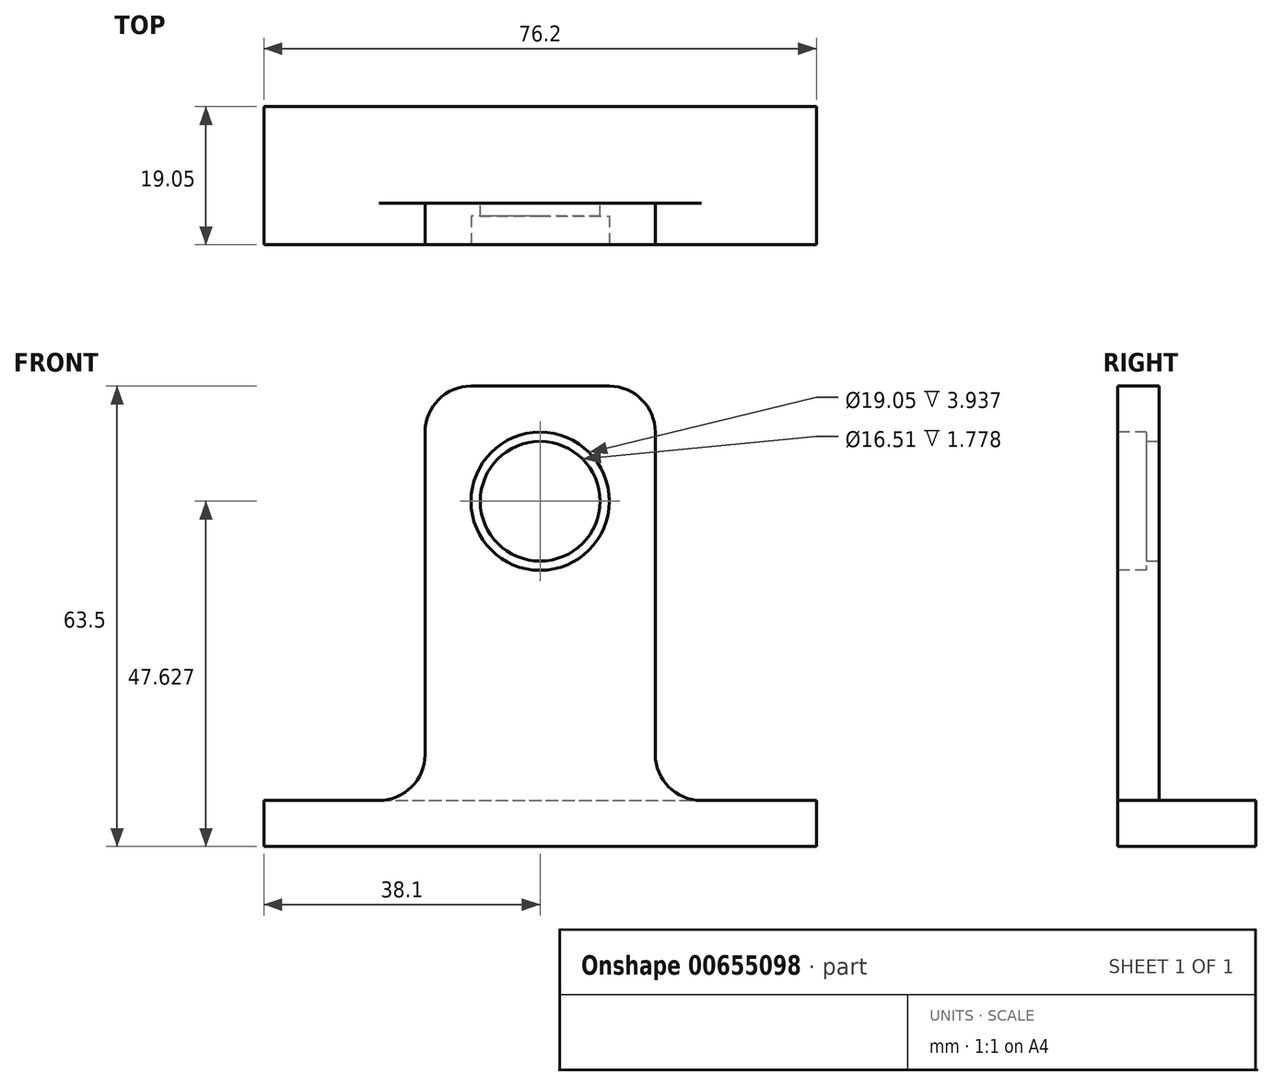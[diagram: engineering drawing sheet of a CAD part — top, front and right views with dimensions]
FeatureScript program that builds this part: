
annotation { "Feature Type Name" : "Feature", "Feature Type Description" : "" }
export const myFeature = defineFeature(function(context is Context, id is Id, definition is map)
    precondition{}
    {
        {
            var Q0;
            Q0=qCreatedBy(makeId("Front.planeOp"),FACE);
            var sketch = newSketch(context, id + "F0", { "sketchPlane" : qUnion([Q0])});
            skLineSegment(sketch, "E0.bottom", {"start": v(-38.1, -49.67) * mm, "end": v(38.1, -49.67) * mm});
            skLineSegment(sketch, "E0.top", {"start": v(22.23, -43.32) * mm, "end": v(38.1, -43.32) * mm});
            skLineSegment(sketch, "E0.left", {"start": v(-38.1, -49.67) * mm, "end": v(-38.1, -43.32) * mm});
            skLineSegment(sketch, "E0.right", {"start": v(38.1, -49.67) * mm, "end": v(38.1, -43.32) * mm});
            skLineSegment(sketch, "E1.top", {"start": v(-9.53, 13.83) * mm, "end": v(9.52, 13.83) * mm});
            skLineSegment(sketch, "E1.left", {"start": v(-15.87, -36.97) * mm, "end": v(-15.88, 7.48) * mm});
            skLineSegment(sketch, "E1.right", {"start": v(15.88, -36.97) * mm, "end": v(15.88, 7.48) * mm});
            skPoint(sketch, "E2.visualSharp", {"position": v(-15.88, 13.83) * mm});
            skArc(sketch, "E2.filletArc", {"start": v(-9.53, 13.83) * mm, "mid": v(-14.02, 11.97) * mm, "end": v(-15.88, 7.48) * mm});
            skPoint(sketch, "E3.visualSharp", {"position": v(15.88, 13.83) * mm});
            skArc(sketch, "E3.filletArc", {"start": v(15.88, 7.48) * mm, "mid": v(14.02, 11.97) * mm, "end": v(9.52, 13.83) * mm});
            skArc(sketch, "E4.filletArc", {"start": v(15.88, -36.97) * mm, "mid": v(17.73, -41.46) * mm, "end": v(22.23, -43.32) * mm});
            skLineSegment(sketch, "E5", {"start": v(-38.1, -43.32) * mm, "end": v(-22.22, -43.32) * mm});
            skPoint(sketch, "E6.visualSharp", {"position": v(-15.87, -43.32) * mm});
            skArc(sketch, "E6.filletArc", {"start": v(-22.22, -43.32) * mm, "mid": v(-17.73, -41.46) * mm, "end": v(-15.87, -36.97) * mm});
            skSolve(sketch);
        }
        {
            var Q0;
            Q0 = qSketchRegion(id + "F0", true);
            extrude(context, id + "F1", {"entities" : qUnion([Q0]), "depth" : 19.05 * mm, "offsetDistance" : 25.4 * mm});
        }
        {
            var Q0;
            Q0=qCreatedBy(makeId("Right.planeOp"),FACE);
            var sketch = newSketch(context, id + "F2", { "sketchPlane" : qUnion([Q0])});
            skLineSegment(sketch, "E7.bottom", {"start": v(-13.33, -43.32) * mm, "end": v(12.83, -43.32) * mm});
            skLineSegment(sketch, "E7.top", {"start": v(-13.34, 13.83) * mm, "end": v(12.83, 13.83) * mm});
            skLineSegment(sketch, "E7.left", {"start": v(-13.33, -43.32) * mm, "end": v(-13.34, 13.83) * mm});
            skLineSegment(sketch, "E7.right", {"start": v(12.83, -43.32) * mm, "end": v(12.83, 13.83) * mm});
            skSolve(sketch);
        }
        {
            var Q0;
            Q0 = qSketchRegion(id + "F2", true);
            extrude(context, id + "F3", {"entities" : qUnion([Q0]), "operationType" : NewBodyOperationType.REMOVE, "endBound" : BoundingType.THROUGH_ALL, "oppositeDirection" : true, "depth" : 25.4 * mm, "offsetDistance" : 25.4 * mm, "hasSecondDirection" : true, "secondDirectionBound" : SecondDirectionBoundingType.THROUGH_ALL, "secondDirectionOppositeDirection" : false, "secondDirectionDepth" : 25.4 * mm});
        }
        {
            var Q0;
            Q0=makeQuery(id+"F1.opExtrude","CAP_FACE",FACE,{"disambiguationData":[OSD([sQuery(id+"F0.wireOp",EDGE,"E0.bottom"),sQuery(id+"F0.wireOp",EDGE,"E0.top"),sQuery(id+"F0.wireOp",EDGE,"E0.left"),sQuery(id+"F0.wireOp",EDGE,"E0.right"),sQuery(id+"F0.wireOp",EDGE,"E1.top"),sQuery(id+"F0.wireOp",EDGE,"E1.left"),sQuery(id+"F0.wireOp",EDGE,"E1.right"),sQuery(id+"F0.wireOp",EDGE,"E2.filletArc"),sQuery(id+"F0.wireOp",EDGE,"E3.filletArc"),sQuery(id+"F0.wireOp",EDGE,"E4.filletArc"),sQuery(id+"F0.wireOp",EDGE,"E5"),sQuery(id+"F0.wireOp",EDGE,"E6.filletArc")])],"isStart":false});
            var sketch = newSketch(context, id + "F4", { "sketchPlane" : qUnion([Q0])});
            skCircle(sketch, "E8", {"center": v(0, -2.04) * mm, "radius": 9.53 * mm});
            skSolve(sketch);
        }
        {
            var Q0;
            Q0 = qSketchRegion(id + "F4", true);
            extrude(context, id + "F5", {"entities" : qUnion([Q0]), "operationType" : NewBodyOperationType.REMOVE, "endBound" : BoundingType.THROUGH_ALL, "oppositeDirection" : true, "depth" : 25.4 * mm, "offsetDistance" : 25.4 * mm});
        }
        {
            var Q0;
            Q0=makeQuery(id+"F3.boolean.opBoolean","COPY",FACE,{"derivedFrom":makeQuery(id+"F3.opExtrude","SWEPT_FACE",FACE,{"disambiguationData":[OSD([sQuery(id+"F2.wireOp",EDGE,"E7.left")])]})});
            var sketch = newSketch(context, id + "F6", { "sketchPlane" : qUnion([Q0])});
            skCircle(sketch, "E9", {"center": v(0, -2.04) * mm, "radius": 8.26 * mm});
            skCircle(sketch, "E10", {"center": v(0, -2.04) * mm, "radius": 9.53 * mm});
            skSolve(sketch);
        }
        {
            var Q0;
            Q0 = qSketchRegion(id + "F6", true);
            extrude(context, id + "F7", {"entities" : qUnion([Q0]), "operationType" : NewBodyOperationType.ADD, "oppositeDirection" : true, "depth" : 1.78 * mm, "offsetDistance" : 25.4 * mm});
        }
    });
